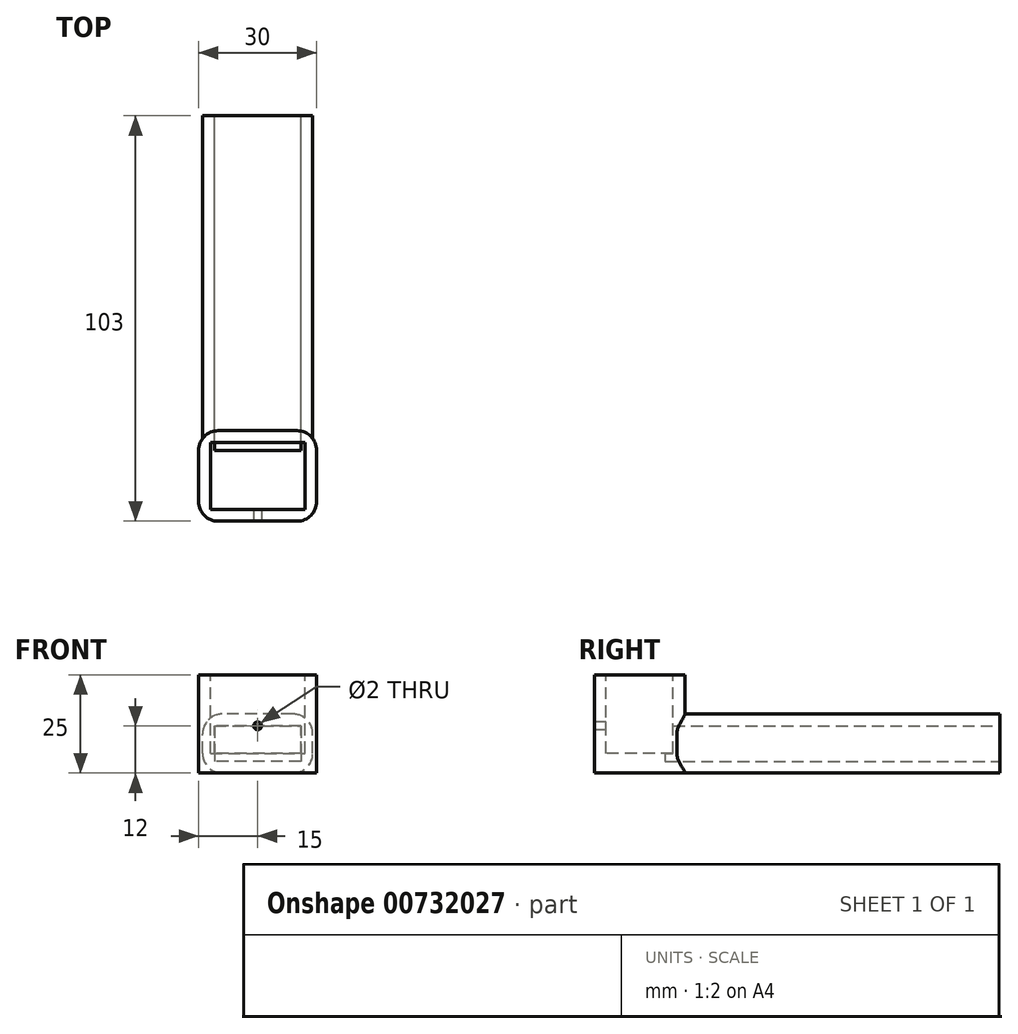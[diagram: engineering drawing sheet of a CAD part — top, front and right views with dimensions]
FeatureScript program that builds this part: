
annotation { "Feature Type Name" : "Feature", "Feature Type Description" : "" }
export const myFeature = defineFeature(function(context is Context, id is Id, definition is map)
    precondition{}
    {
        {
            var Q0;
            Q0=qCreatedBy(makeId("Top.planeOp"),FACE);
            var sketch = newSketch(context, id + "F0", { "sketchPlane" : qUnion([Q0])});
            skLineSegment(sketch, "E0.bottom", {"start": v(-15, 11.5) * mm, "end": v(15, 11.5) * mm});
            skLineSegment(sketch, "E0.top", {"start": v(-15, -11.5) * mm, "end": v(15, -11.5) * mm});
            skLineSegment(sketch, "E0.left", {"start": v(-15, 11.5) * mm, "end": v(-15, -11.5) * mm});
            skLineSegment(sketch, "E0.right", {"start": v(15, 11.5) * mm, "end": v(15, -11.5) * mm});
            skPoint(sketch, "E0.middle", {"position": v(0, 0) * mm});
            skSolve(sketch);
        }
        {
            var Q0;
            Q0 = qSketchRegion(id + "F0", true);
            extrude(context, id + "F1", {"entities" : qUnion([Q0]), "depth" : 25 * mm, "offsetDistance" : 25 * mm});
        }
        {
            var Q0;
            Q0=makeQuery(id+"F1.opExtrude","CAP_FACE",FACE,{"disambiguationData":[OSD([sQuery(id+"F0.wireOp",EDGE,"E0.bottom"),sQuery(id+"F0.wireOp",EDGE,"E0.top"),sQuery(id+"F0.wireOp",EDGE,"E0.left"),sQuery(id+"F0.wireOp",EDGE,"E0.right")])],"isStart":false});
            var sketch = newSketch(context, id + "F2", { "sketchPlane" : qUnion([Q0])});
            skLineSegment(sketch, "E1.bottom", {"start": v(-12, 8.5) * mm, "end": v(12, 8.5) * mm});
            skLineSegment(sketch, "E1.top", {"start": v(-12, -8.5) * mm, "end": v(12, -8.5) * mm});
            skLineSegment(sketch, "E1.left", {"start": v(-12, 8.5) * mm, "end": v(-12, -8.5) * mm});
            skLineSegment(sketch, "E1.right", {"start": v(12, 8.5) * mm, "end": v(12, -8.5) * mm});
            skPoint(sketch, "E1.middle", {"position": v(0, 0) * mm});
            skSolve(sketch);
        }
        {
            var Q0;
            Q0 = qSketchRegion(id + "F2", true);
            extrude(context, id + "F3", {"entities" : qUnion([Q0]), "operationType" : NewBodyOperationType.REMOVE, "oppositeDirection" : true, "depth" : 20 * mm, "offsetDistance" : 25 * mm});
        }
        {
            var Q0;
            Q0=makeQuery(id+"F1.opExtrude","SWEPT_EDGE",EDGE,{"disambiguationData":[OSD([sQuery(id+"F0.wireOp",EDGE,"E0.top"),sQuery(id+"F0.wireOp",EDGE,"E0.right")])]});
            var Q1;
            Q1=makeQuery(id+"F1.opExtrude","SWEPT_EDGE",EDGE,{"disambiguationData":[OSD([sQuery(id+"F0.wireOp",EDGE,"E0.bottom"),sQuery(id+"F0.wireOp",EDGE,"E0.right")])]});
            var Q2;
            Q2=makeQuery(id+"F1.opExtrude","SWEPT_EDGE",EDGE,{"disambiguationData":[OSD([sQuery(id+"F0.wireOp",EDGE,"E0.top"),sQuery(id+"F0.wireOp",EDGE,"E0.left")])]});
            var Q3;
            Q3=makeQuery(id+"F1.opExtrude","SWEPT_EDGE",EDGE,{"disambiguationData":[OSD([sQuery(id+"F0.wireOp",EDGE,"E0.bottom"),sQuery(id+"F0.wireOp",EDGE,"E0.left")])]});
            fillet(context, id + "F4", {"entities" : qUnion([Q0, Q1, Q2, Q3]), "radius" : 5 * mm, "tangentPropagation" : true, "allowEdgeOverflow" : false});
        }
        {
            var Q0;
            Q0=makeQuery(id+"F1.opExtrude","SWEPT_FACE",FACE,{"disambiguationData":[OSD([sQuery(id+"F0.wireOp",EDGE,"E0.top")])]});
            var sketch = newSketch(context, id + "F5", { "sketchPlane" : qUnion([Q0])});
            skCircle(sketch, "E2", {"center": v(0, 12) * mm, "radius": 1 * mm});
            skSolve(sketch);
        }
        {
            var Q0;
            Q0=makeQuery(id+"F5.imprint","IMPRINT",FACE,{"disambiguationData":[TD([[makeQuery(id+"F5.imprint","IMPRINT",EDGE,{"derivedFrom":sQuery(id+"F5.wireOp",EDGE,"E2")}),1.0]])]});
            extrude(context, id + "F6", {"entities" : qUnion([Q0]), "operationType" : NewBodyOperationType.REMOVE, "oppositeDirection" : true, "depth" : 4 * mm, "offsetDistance" : 25 * mm});
        }
        {
            var Q0;
            Q0=makeQuery(id+"F1.opExtrude","SWEPT_FACE",FACE,{"disambiguationData":[OSD([sQuery(id+"F0.wireOp",EDGE,"E0.bottom")])]});
            var sketch = newSketch(context, id + "F7", { "sketchPlane" : qUnion([Q0])});
            skLineSegment(sketch, "E3.bottom", {"start": v(-14, 0) * mm, "end": v(14, 0) * mm});
            skLineSegment(sketch, "E3.top", {"start": v(-14, 15) * mm, "end": v(14, 15) * mm});
            skLineSegment(sketch, "E3.left", {"start": v(-14, 0) * mm, "end": v(-14, 15) * mm});
            skLineSegment(sketch, "E3.right", {"start": v(14, 0) * mm, "end": v(14, 15) * mm});
            skPoint(sketch, "E3.middle", {"position": v(0, 7.5) * mm});
            skSolve(sketch);
        }
        {
            var Q0;
            Q0 = qSketchRegion(id + "F7", true);
            extrude(context, id + "F8", {"entities" : qUnion([Q0]), "operationType" : NewBodyOperationType.ADD, "depth" : 80 * mm, "offsetDistance" : 25 * mm});
        }
        {
            var Q0;
            {var subQ0=sQuery(id+"F7.wireOp",EDGE,"E3.bottom");var subQ3=sQuery(id+"F7.wireOp",EDGE,"E3.top");var subQ4=sQuery(id+"F7.wireOp",EDGE,"E3.left");Q0=makeQuery(id+"F8.boolean.opBoolean","SPLIT",FACE,{"disambiguationData":[TD([makeQuery(id+"F8.opExtrude","SWEPT_FACE",FACE,{"disambiguationData":[OSD([subQ4])]})])],"derivedFrom":makeQuery(id+"F8.opExtrude","CAP_FACE",FACE,{"disambiguationData":[OSD([subQ0,subQ3,subQ4,sQuery(id+"F7.wireOp",EDGE,"E3.right")])],"isStart":true})});}
            extrude(context, id + "F9", {"entities" : qUnion([Q0]), "operationType" : NewBodyOperationType.ADD, "depth" : 2 * mm, "offsetDistance" : 25 * mm});
        }
        {
            var Q0;
            Q0=makeQuery(id+"F8.opExtrude","CAP_FACE",FACE,{"disambiguationData":[OSD([sQuery(id+"F7.wireOp",EDGE,"E3.bottom"),sQuery(id+"F7.wireOp",EDGE,"E3.top"),sQuery(id+"F7.wireOp",EDGE,"E3.left"),sQuery(id+"F7.wireOp",EDGE,"E3.right")])],"isStart":false});
            var sketch = newSketch(context, id + "F10", { "sketchPlane" : qUnion([Q0])});
            skLineSegment(sketch, "E4.bottom", {"start": v(-11, 12) * mm, "end": v(11, 12) * mm});
            skLineSegment(sketch, "E4.top", {"start": v(-11, 3) * mm, "end": v(11, 3) * mm});
            skLineSegment(sketch, "E4.left", {"start": v(-11, 12) * mm, "end": v(-11, 3) * mm});
            skLineSegment(sketch, "E4.right", {"start": v(11, 12) * mm, "end": v(11, 3) * mm});
            skPoint(sketch, "E4.middle", {"position": v(0, 7.5) * mm});
            skPoint(sketch, "E4.middle.positionSnap0", {"position": v(-14, 7.5) * mm});
            skPoint(sketch, "E4.centerSnap0", {"position": v(-14, 7.5) * mm});
            skSolve(sketch);
        }
        {
            var Q0;
            Q0 = qSketchRegion(id + "F10", true);
            extrude(context, id + "F11", {"entities" : qUnion([Q0]), "operationType" : NewBodyOperationType.REMOVE, "oppositeDirection" : true, "depth" : 85 * mm, "offsetDistance" : 25 * mm});
        }
        {
            var Q0;
            {var subQ0=sQuery(id+"F7.wireOp",EDGE,"E3.bottom");var subQ3=sQuery(id+"F7.wireOp",EDGE,"E3.right");var subQ4=sQuery(id+"F7.wireOp",EDGE,"E3.top");Q0=makeQuery(id+"F8.boolean.opBoolean","SPLIT",FACE,{"disambiguationData":[TD([makeQuery(id+"F8.opExtrude","SWEPT_FACE",FACE,{"disambiguationData":[OSD([subQ3])]})])],"derivedFrom":makeQuery(id+"F8.opExtrude","CAP_FACE",FACE,{"disambiguationData":[OSD([subQ0,subQ4,sQuery(id+"F7.wireOp",EDGE,"E3.left"),subQ3])],"isStart":true})});}
            extrude(context, id + "F12", {"entities" : qUnion([Q0]), "operationType" : NewBodyOperationType.ADD, "depth" : 3 * mm, "offsetDistance" : 25 * mm});
        }
        {
            var Q0;
            {var subQ0=sQuery(id+"F7.wireOp",EDGE,"E3.right");var subQ1=sQuery(id+"F7.wireOp",EDGE,"E3.top");Q0=makeQuery(id+"F12.boolean.opBoolean","MERGE",EDGE,{"derivedFrom":[makeQuery(id+"F8.opExtrude","SWEPT_EDGE",EDGE,{"disambiguationData":[OSD([subQ1,subQ0])]}),makeQuery(id+"F12.opExtrude","SWEPT_EDGE",EDGE,{"disambiguationData":[OSD([subQ1,subQ0])]})]});}
            var Q1;
            {var subQ0=sQuery(id+"F7.wireOp",EDGE,"E3.right");var subQ1=sQuery(id+"F7.wireOp",EDGE,"E3.bottom");Q1=makeQuery(id+"F12.boolean.opBoolean","MERGE",EDGE,{"derivedFrom":[makeQuery(id+"F8.opExtrude","SWEPT_EDGE",EDGE,{"disambiguationData":[OSD([subQ1,subQ0])]}),makeQuery(id+"F12.opExtrude","SWEPT_EDGE",EDGE,{"disambiguationData":[OSD([subQ1,subQ0])]})]});}
            var Q2;
            {var subQ0=sQuery(id+"F7.wireOp",EDGE,"E3.left");var subQ1=sQuery(id+"F7.wireOp",EDGE,"E3.top");Q2=makeQuery(id+"F9.boolean.opBoolean","MERGE",EDGE,{"derivedFrom":[makeQuery(id+"F8.opExtrude","SWEPT_EDGE",EDGE,{"disambiguationData":[OSD([subQ1,subQ0])]}),makeQuery(id+"F9.opExtrude","SWEPT_EDGE",EDGE,{"disambiguationData":[OSD([subQ1,subQ0])]})]});}
            var Q3;
            {var subQ0=sQuery(id+"F7.wireOp",EDGE,"E3.left");var subQ1=sQuery(id+"F7.wireOp",EDGE,"E3.bottom");Q3=makeQuery(id+"F9.boolean.opBoolean","MERGE",EDGE,{"derivedFrom":[makeQuery(id+"F8.opExtrude","SWEPT_EDGE",EDGE,{"disambiguationData":[OSD([subQ1,subQ0])]}),makeQuery(id+"F9.opExtrude","SWEPT_EDGE",EDGE,{"disambiguationData":[OSD([subQ1,subQ0])]})]});}
            var Q4;
            Q4=makeQuery(id+"F3.boolean.opBoolean","COPY",EDGE,{"derivedFrom":makeQuery(id+"F3.opExtrude","CAP_EDGE",EDGE,{"disambiguationData":[OSD([sQuery(id+"F2.wireOp",EDGE,"E1.top")])],"isStart":true})});
            var Q5;
            Q5=makeQuery(id+"F3.boolean.opBoolean","COPY",EDGE,{"derivedFrom":makeQuery(id+"F3.opExtrude","CAP_EDGE",EDGE,{"disambiguationData":[OSD([sQuery(id+"F2.wireOp",EDGE,"E1.left")])],"isStart":true})});
            var Q6;
            Q6=makeQuery(id+"F3.boolean.opBoolean","COPY",EDGE,{"derivedFrom":makeQuery(id+"F3.opExtrude","CAP_EDGE",EDGE,{"disambiguationData":[OSD([sQuery(id+"F2.wireOp",EDGE,"E1.bottom")])],"isStart":true})});
            var Q7;
            Q7=makeQuery(id+"F3.boolean.opBoolean","COPY",EDGE,{"derivedFrom":makeQuery(id+"F3.opExtrude","CAP_EDGE",EDGE,{"disambiguationData":[OSD([sQuery(id+"F2.wireOp",EDGE,"E1.right")])],"isStart":true})});
            fillet(context, id + "F13", {"entities" : qUnion([Q0, Q1, Q2, Q3, Q4, Q5, Q6, Q7]), "radius" : 5 * mm, "tangentPropagation" : true, "allowEdgeOverflow" : false});
        }
    });
